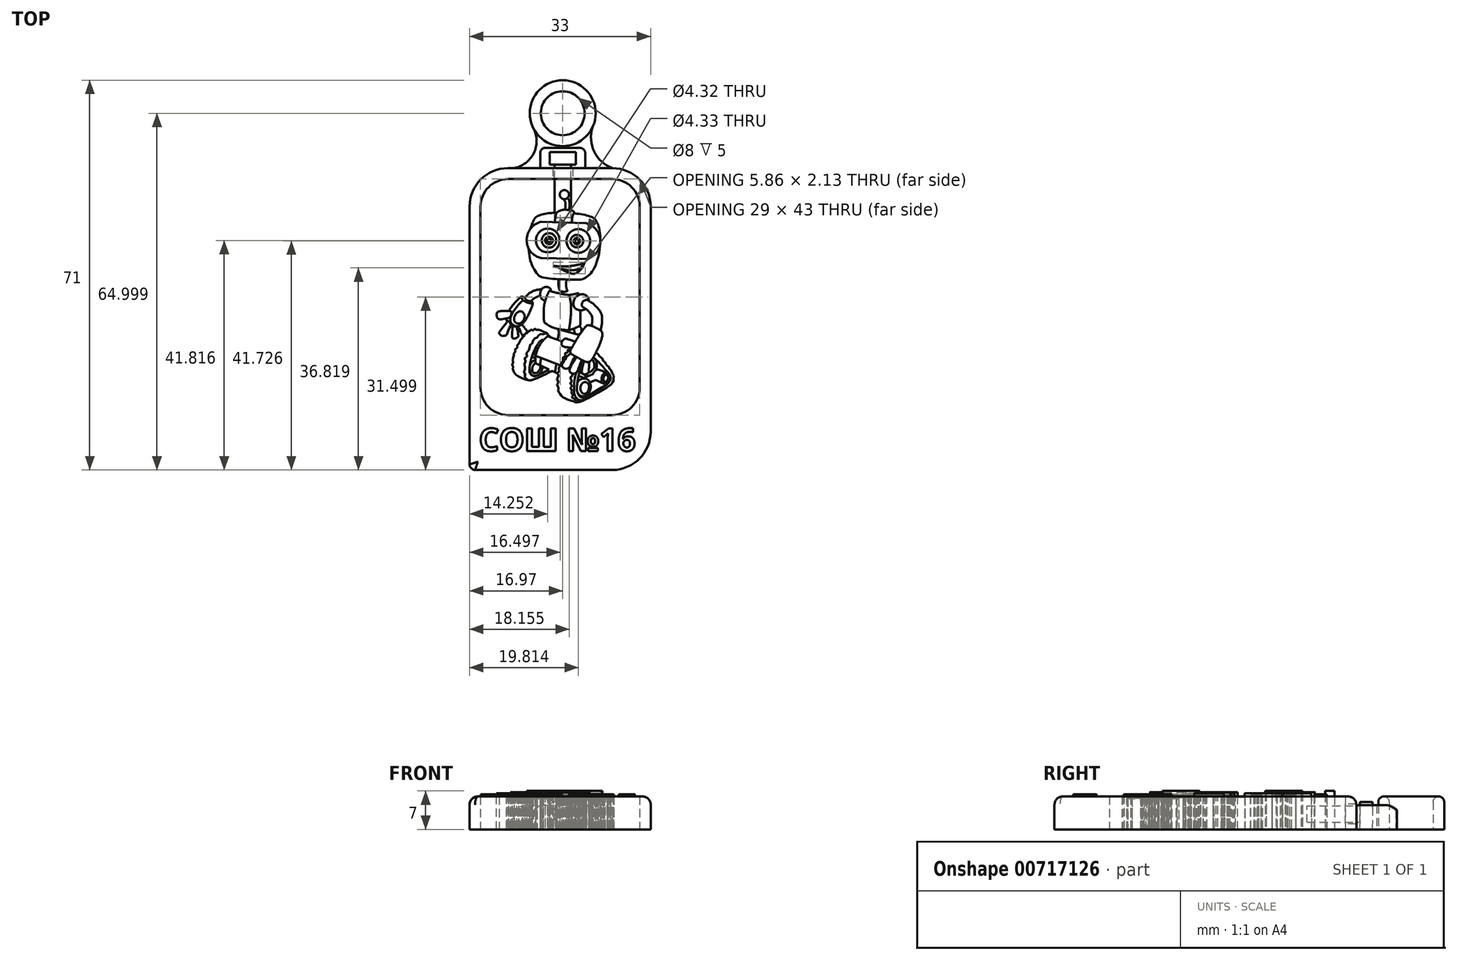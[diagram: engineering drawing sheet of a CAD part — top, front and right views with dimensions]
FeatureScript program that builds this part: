
annotation { "Feature Type Name" : "Feature", "Feature Type Description" : "" }
export const myFeature = defineFeature(function(context is Context, id is Id, definition is map)
    precondition{}
    {
        {
            var Q0;
            Q0=qCreatedBy(makeId("Top.planeOp"),FACE);
            var sketch = newSketch(context, id + "F0", { "sketchPlane" : qUnion([Q0])});
            skCircle(sketch, "E0", {"center": v(0.3, 18.7) * mm, "radius": 0.83 * mm});
            skFitSpline(sketch, "E1", {"points": [v(0.12, 17.9) * mm, v(0.47, 17.38) * mm, v(0.44, 15.96) * mm], "startDerivative": vector(0.9, -1.14) * mm, "endDerivative": vector(-0.07, -2.7) * mm});
            skFitSpline(sketch, "E2", {"points": [v(0.91, 18.15) * mm, v(1.19, 17.54) * mm, v(1.2, 15.9) * mm], "startDerivative": vector(0.78, -1.27) * mm, "endDerivative": vector(-0.02, -2.88) * mm});
            skCircle(sketch, "E3", {"center": v(-2.5, 10.36) * mm, "radius": 0.33 * mm});
            skCircle(sketch, "E4", {"center": v(-2.5, 10.36) * mm, "radius": 0.69 * mm});
            skCircle(sketch, "E5", {"center": v(-2.5, 10.36) * mm, "radius": 1.31 * mm});
            skCircle(sketch, "E6", {"center": v(2.58, 10.23) * mm, "radius": 0.33 * mm});
            skCircle(sketch, "E7", {"center": v(2.58, 10.23) * mm, "radius": 0.59 * mm});
            skCircle(sketch, "E8", {"center": v(2.58, 10.23) * mm, "radius": 1.15 * mm});
            skCircle(sketch, "E9", {"center": v(2.84, 10.27) * mm, "radius": 2.16 * mm});
            skPoint(sketch, "E9.first.point", {"position": v(4.19, 8.57) * mm});
            skPoint(sketch, "E9.second.point", {"position": v(4.6, 11.53) * mm});
            skPoint(sketch, "E9.third.point", {"position": v(0.83, 11.06) * mm});
            skCircle(sketch, "E10", {"center": v(-2.72, 10.36) * mm, "radius": 2.16 * mm});
            skPoint(sketch, "E10.first.point", {"position": v(-4.8, 10.92) * mm});
            skPoint(sketch, "E10.second.point", {"position": v(-3.27, 8.27) * mm});
            skPoint(sketch, "E10.third.point", {"position": v(-0.74, 11.23) * mm});
            skArc(sketch, "E11", {"start": v(-3.9, 13.75) * mm, "mid": v(-6.58, 10.45) * mm, "end": v(-3.92, 7.14) * mm});
            skArc(sketch, "E12", {"start": v(4.26, 6.95) * mm, "mid": v(6.85, 10.2) * mm, "end": v(4.28, 13.48) * mm});
            skLineSegment(sketch, "E13", {"start": v(-3.9, 13.75) * mm, "end": v(4.28, 13.48) * mm});
            skLineSegment(sketch, "E14", {"start": v(4.26, 6.95) * mm, "end": v(-3.92, 7.14) * mm});
            skFitSpline(sketch, "E15", {"points": [v(-1.45, 13.67) * mm, v(-1.34, 14.52) * mm, v(-1.2, 15.22) * mm, v(-1.1, 15.44) * mm, v(-0.38, 15.83) * mm, v(0.25, 15.96) * mm, v(0.44, 15.96) * mm, v(1.6, 15.83) * mm, v(2.03, 15.62) * mm, v(2.14, 15.45) * mm, v(2.16, 15.35) * mm, v(2.13, 15.29) * mm, v(2.02, 15.27) * mm, v(1.88, 15.13) * mm, v(1.62, 13.57) * mm], "startDerivative": vector(0.63, 8.93) * mm, "endDerivative": vector(-1.73, -15.25) * mm});
            skFitSpline(sketch, "E16", {"points": [v(-5.9, 12.47) * mm, v(-5.25, 14.1) * mm, v(-4.61, 14.77) * mm, v(-2.92, 15.27) * mm, v(-1.14, 15.4) * mm], "startDerivative": vector(2.4, 6.84) * mm, "endDerivative": vector(6.47, 0.13) * mm});
            skFitSpline(sketch, "E17", {"points": [v(-6.22, 8.92) * mm, v(-5.75, 6.26) * mm, v(-4.69, 4.3) * mm, v(-4.2, 3.84) * mm, v(-2.5, 3.43) * mm, v(0.92, 3.23) * mm, v(3.35, 3.25) * mm, v(4.25, 3.62) * mm, v(5.1, 4.38) * mm, v(6.1, 6.12) * mm, v(6.84, 10.02) * mm, v(6.6, 12.73) * mm, v(6.13, 13.9) * mm, v(5.7, 14.4) * mm, v(5.07, 14.7) * mm, v(3.8, 15.05) * mm, v(2.13, 15.29) * mm], "startDerivative": vector(2.92, -34.4) * mm, "endDerivative": vector(-27.68, 3.02) * mm});
            skFitSpline(sketch, "E18", {"points": [v(-1.75, 5.73) * mm, v(0.46, 5.61) * mm, v(2.53, 5.87) * mm, v(3.44, 6.09) * mm, v(4.12, 6.42) * mm], "startDerivative": vector(6.97, -0.72) * mm, "endDerivative": vector(3.62, 2.06) * mm});
            skFitSpline(sketch, "E19", {"points": [v(-1.75, 5.73) * mm, v(-0.96, 5.5) * mm, v(-0.2, 5.08) * mm, v(0.9, 4.56) * mm, v(1.74, 4.3) * mm, v(2.27, 4.34) * mm, v(3.1, 4.89) * mm, v(3.8, 5.89) * mm, v(3.9, 6.18) * mm, v(4.12, 6.42) * mm], "startDerivative": vector(7, -1.48) * mm, "endDerivative": vector(3.55, 3.32) * mm});
            skFitSpline(sketch, "E20", {"points": [v(-0.14, 5.6) * mm, v(-0.03, 5.1) * mm], "startDerivative": vector(0.1, -0.52) * mm, "endDerivative": vector(0.1, -0.52) * mm});
            skFitSpline(sketch, "E21", {"points": [v(-0.03, 5.1) * mm, v(0.8, 4.95) * mm, v(1.93, 4.94) * mm, v(2.96, 5.2) * mm, v(3.46, 5.49) * mm], "startDerivative": vector(3.26, -0.68) * mm, "endDerivative": vector(2.23, 1.53) * mm});
            skFitSpline(sketch, "E22", {"points": [v(3.46, 5.49) * mm, v(3.57, 6.14) * mm], "startDerivative": vector(0.1, 0.65) * mm, "endDerivative": vector(0.1, 0.65) * mm});
            skFitSpline(sketch, "E23", {"points": [v(-0.7, 1.73) * mm, v(-1, 1.68) * mm, v(-1.52, 1.57) * mm, v(-2.17, 1.34) * mm, v(-2.34, 1.21) * mm, v(-1.9, 1.02) * mm, v(-0.46, 0.67) * mm, v(0.7, 0.47) * mm, v(1.12, 0.44) * mm, v(1.38, 0.45) * mm, v(1.8, 0.52) * mm, v(2.6, 0.69) * mm, v(2.77, 0.77) * mm, v(2.73, 0.86) * mm, v(2.54, 1.01) * mm, v(1.61, 1.37) * mm, v(0.7, 1.58) * mm], "startDerivative": vector(-6.76, -0.7) * mm, "endDerivative": vector(-10.1, 1.55) * mm});
            skFitSpline(sketch, "E24", {"points": [v(-0.76, 3.3) * mm, v(-0.8, 2.67) * mm, v(-0.75, 1.97) * mm, v(-0.57, 1.3) * mm, v(-0.45, 1.13) * mm], "startDerivative": vector(-0.24, -2.28) * mm, "endDerivative": vector(0.93, -0.81) * mm});
            skFitSpline(sketch, "E25", {"points": [v(0.74, 3.24) * mm, v(0.64, 2.9) * mm, v(0.6, 2.27) * mm, v(0.66, 1.73) * mm, v(0.81, 1.31) * mm, v(0.85, 1.18) * mm], "startDerivative": vector(-0.63, -1.61) * mm, "endDerivative": vector(-0.1, -1.03) * mm});
            skFitSpline(sketch, "E26", {"points": [v(-0.45, 1.13) * mm, v(-0.22, 1.06) * mm, v(0.33, 1.01) * mm, v(0.7, 1.09) * mm, v(0.85, 1.18) * mm], "startDerivative": vector(0.96, -0.5) * mm, "endDerivative": vector(0.36, 0.85) * mm});
            skFitSpline(sketch, "E27", {"points": [v(1.12, 0.44) * mm, v(1.24, 0.2) * mm, v(1.38, -0.41) * mm, v(1.53, -1.74) * mm, v(1.38, -4.22) * mm, v(1.12, -5.92) * mm, v(1.04, -6) * mm, v(0.22, -5.93) * mm, v(-1.19, -5.72) * mm, v(-2.27, -5.29) * mm, v(-3.16, -4.72) * mm, v(-3.32, -4.57) * mm, v(-3.39, -4.44) * mm, v(-3.47, -3.34) * mm, v(-3.46, -2.3) * mm, v(-3.3, -1.07) * mm, v(-2.8, 0.44) * mm, v(-2.44, 1.14) * mm, v(-2.33, 1.25) * mm], "startDerivative": vector(7.24, -3.6) * mm, "endDerivative": vector(4.32, 3.3) * mm});
            skFitSpline(sketch, "E28", {"points": [v(1.04, -6) * mm, v(1.39, -5.9) * mm, v(2.36, -5.56) * mm, v(2.9, -5.32) * mm, v(3.1, -5.2) * mm, v(3.18, -5) * mm, v(3.21, -4.58) * mm, v(3.19, -2.37) * mm], "startDerivative": vector(2.66, 0.6) * mm, "endDerivative": vector(-0.15, 9.68) * mm});
            skFitSpline(sketch, "E29", {"points": [v(2.77, 0.79) * mm, v(2.82, 0.7) * mm, v(2.87, 0.37) * mm], "startDerivative": vector(0.07, -0.11) * mm, "endDerivative": vector(0.06, -0.59) * mm});
            skFitSpline(sketch, "E30", {"points": [v(-3.17, -0.58) * mm, v(-3.39, -0.55) * mm, v(-3.82, -0.28) * mm, v(-4.1, 0.29) * mm, v(-4.04, 1.06) * mm, v(-3.73, 1.58) * mm, v(-3.27, 1.86) * mm, v(-2.76, 1.88) * mm, v(-2.36, 1.68) * mm, v(-2.22, 1.54) * mm, v(-2.11, 1.36) * mm], "startDerivative": vector(-2.86, 0.03) * mm, "endDerivative": vector(1.55, -2.75) * mm});
            skFitSpline(sketch, "E31", {"points": [v(4.2, -2.1) * mm, v(3.83, -2.28) * mm, v(3.38, -2.4) * mm, v(3.19, -2.37) * mm, v(2.56, -2.2) * mm, v(2.14, -1.83) * mm, v(1.93, -1.09) * mm, v(2.2, -0.2) * mm, v(2.56, 0.19) * mm, v(2.87, 0.37) * mm, v(3.37, 0.54) * mm, v(4, 0.47) * mm, v(4.49, 0.12) * mm, v(4.73, -0.35) * mm, v(4.76, -0.66) * mm], "startDerivative": vector(-4.5, -3.3) * mm, "endDerivative": vector(0.01, -5.32) * mm});
            skFitSpline(sketch, "E32", {"points": [v(-3.48, -3.22) * mm, v(-1.78, -4.06) * mm, v(1.36, -4.43) * mm, v(3.2, -3.79) * mm], "startDerivative": vector(4.9, -3.02) * mm, "endDerivative": vector(5.37, 2.7) * mm});
            skFitSpline(sketch, "E33", {"points": [v(-3.84, 1.46) * mm, v(-4.94, 1.3) * mm, v(-6.15, 0.68) * mm, v(-6.87, -0.09) * mm], "startDerivative": vector(-3.3, -0.27) * mm, "endDerivative": vector(-2.02, -2.53) * mm});
            skFitSpline(sketch, "E34", {"points": [v(-4.08, 0.2) * mm, v(-4.4, 0.17) * mm, v(-5.23, -0.2) * mm, v(-5.69, -0.66) * mm], "startDerivative": vector(-1.12, 0.03) * mm, "endDerivative": vector(-1.09, -1.4) * mm});
            skFitSpline(sketch, "E35", {"points": [v(-6.87, -0.09) * mm, v(-6.78, -0.35) * mm, v(-6.22, -0.66) * mm, v(-5.8, -0.72) * mm, v(-5.69, -0.66) * mm], "startDerivative": vector(0.17, -1.2) * mm, "endDerivative": vector(0.62, 0.48) * mm});
            skFitSpline(sketch, "E36", {"points": [v(-5.65, -0.61) * mm, v(-5.52, -0.96) * mm, v(-5.55, -1.08) * mm, v(-5.79, -1.1) * mm, v(-6.43, -0.95) * mm, v(-7.26, -0.55) * mm, v(-7.32, -0.47) * mm, v(-7.53, 0.04) * mm, v(-7.46, 0.1) * mm, v(-6.84, -0.04) * mm], "startDerivative": vector(1.46, -3.36) * mm, "endDerivative": vector(5.12, -1.6) * mm});
            skFitSpline(sketch, "E37", {"points": [v(-7.4, 0.1) * mm, v(-7.53, 0.13) * mm, v(-7.7, 0.04) * mm, v(-8.25, -0.5) * mm, v(-9.37, -1.76) * mm, v(-9.7, -2.26) * mm, v(-9.85, -2.52) * mm], "startDerivative": vector(-1.54, 0.55) * mm, "endDerivative": vector(-1.06, -1.93) * mm});
            skFitSpline(sketch, "E38", {"points": [v(-5.54, -0.9) * mm, v(-5.48, -1.03) * mm, v(-5.48, -1.23) * mm, v(-6.29, -3.27) * mm, v(-6.98, -4.42) * mm, v(-7.46, -4.94) * mm, v(-8, -5.24) * mm, v(-8.74, -5.2) * mm, v(-9.4, -4.73) * mm, v(-9.52, -3.77) * mm, v(-9.1, -2.76) * mm, v(-8.38, -1.75) * mm, v(-7.3, -0.5) * mm], "startDerivative": vector(2.07, -4.05) * mm, "endDerivative": vector(10.06, 11.15) * mm});
            skEllipse(sketch, "E39", {"center": v(-7.91, -3.7) * mm, "majorRadius": 1.17 * mm, "minorRadius": 0.9 * mm, "majorAxis": v(0.45, 0.9)});
            skFitSpline(sketch, "E40", {"points": [v(-9.85, -3.75) * mm, v(-11.14, -4) * mm, v(-11.6, -4) * mm, v(-11.94, -3.67) * mm, v(-12.06, -3) * mm, v(-11.93, -2.73) * mm, v(-11.68, -2.58) * mm, v(-11.07, -2.52) * mm, v(-9.85, -2.52) * mm], "startDerivative": vector(-8, -1.73) * mm, "endDerivative": vector(7.43, -0.04) * mm});
            skFitSpline(sketch, "E41", {"points": [v(-9.85, -3.75) * mm, v(-9.6, -3.57) * mm, v(-9.39, -3.2) * mm, v(-9.34, -2.7) * mm, v(-9.52, -2.52) * mm, v(-9.85, -2.52) * mm], "startDerivative": vector(1.43, 0.8) * mm, "endDerivative": vector(-1.85, -0.22) * mm});
            skFitSpline(sketch, "E42", {"points": [v(4.38, -0.46) * mm, v(4.76, -0.66) * mm, v(5.4, -1.08) * mm, v(6.04, -1.64) * mm, v(6.54, -2.18) * mm, v(7.06, -3.11) * mm, v(7.16, -4.62) * mm, v(6.9, -6.06) * mm], "startDerivative": vector(3.69, -1.9) * mm, "endDerivative": vector(-2.34, -7.83) * mm});
            skFitSpline(sketch, "E43", {"points": [v(3.66, -1.78) * mm, v(4.2, -2.1) * mm, v(4.87, -2.73) * mm, v(5.32, -3.49) * mm, v(5.34, -4.62) * mm, v(5.24, -5.2) * mm], "startDerivative": vector(2.71, -1.62) * mm, "endDerivative": vector(-1.18, -2.93) * mm});
            skFitSpline(sketch, "E44", {"points": [v(6.9, -6.06) * mm, v(7.16, -6.34) * mm, v(7.23, -6.83) * mm, v(6.74, -8.54) * mm, v(5.58, -10.93) * mm, v(5.1, -11.56) * mm, v(4.63, -11.8) * mm, v(3.71, -11.54) * mm, v(1.8, -10.47) * mm, v(1.45, -10.2) * mm, v(1.37, -9.71) * mm, v(1.59, -9.3) * mm, v(2.54, -7.66) * mm, v(3.61, -6.06) * mm, v(4.2, -5.3) * mm, v(4.43, -5.1) * mm, v(5.24, -5.2) * mm, v(6.9, -6.06) * mm]});
            skFitSpline(sketch, "E45", {"points": [v(2.3, -8.07) * mm, v(0.6, -7.54) * mm, v(0.42, -7.54) * mm, v(0, -7.87) * mm, v(-0.23, -8.54) * mm, v(-0.05, -8.88) * mm, v(0.5, -9.08) * mm, v(1.68, -9.17) * mm], "startDerivative": vector(-9.45, 3.1) * mm, "endDerivative": vector(6.78, -0.26) * mm});
            skFitSpline(sketch, "E46", {"points": [v(3.87, -11.61) * mm, v(3.62, -12.64) * mm, v(3.48, -13.45) * mm, v(3.59, -13.84) * mm, v(3.9, -14.03) * mm, v(4.39, -13.95) * mm, v(4.76, -13.6) * mm, v(4.76, -13.41) * mm, v(4.85, -11.74) * mm], "startDerivative": vector(-1.62, -6.5) * mm, "endDerivative": vector(0.7, 10.55) * mm});
            skFitSpline(sketch, "E47", {"points": [v(3.5, -11.43) * mm, v(2.64, -13.52) * mm, v(2.48, -13.76) * mm, v(1.9, -13.9) * mm, v(1.36, -13.66) * mm, v(1.26, -13.3) * mm, v(1.44, -12.67) * mm, v(2.53, -10.9) * mm], "startDerivative": vector(-4.72, -11.44) * mm, "endDerivative": vector(5.93, 9.05) * mm});
            skFitSpline(sketch, "E48", {"points": [v(2.27, -10.74) * mm, v(1.68, -11.81) * mm, v(1.26, -12.74) * mm, v(0.92, -12.97) * mm, v(0.34, -12.97) * mm, v(-0.14, -12.43) * mm, v(0.2, -11.65) * mm, v(0.86, -10.73) * mm, v(1.45, -10.2) * mm], "startDerivative": vector(-3.77, -6.76) * mm, "endDerivative": vector(4.2, 4.03) * mm});
            skFitSpline(sketch, "E49", {"points": [v(3.66, -1.78) * mm, v(3.48, -1.45) * mm, v(3.71, -0.73) * mm, v(4.38, -0.46) * mm], "startDerivative": vector(-0.94, 1.03) * mm, "endDerivative": vector(1.87, 0.43) * mm});
            skFitSpline(sketch, "E50", {"points": [v(1.6, -9.27) * mm, v(1.43, -9.26) * mm, v(1.38, -9.44) * mm, v(0.97, -9.54) * mm, v(0.86, -10.03) * mm, v(0.46, -10.2) * mm, v(0.48, -10.7) * mm, v(0.05, -10.97) * mm, v(0.07, -11.56) * mm, v(-0.23, -11.9) * mm, v(-0.38, -12.43) * mm, v(-0.7, -12.82) * mm, v(-0.7, -13.5) * mm, v(-0.98, -13.83) * mm, v(-0.79, -14.3) * mm, v(-1.05, -14.84) * mm, v(-0.8, -15.5) * mm, v(-1.05, -15.84) * mm, v(-0.76, -16.5) * mm, v(-0.84, -16.9) * mm, v(-0.46, -17.65) * mm, v(0.2, -18.28) * mm, v(2.04, -19.01) * mm, v(3.13, -19.05) * mm, v(8.56, -16.08) * mm, v(9.01, -15.65) * mm, v(9.15, -15.34) * mm, v(9.27, -15.14) * mm, v(9.21, -14.97) * mm, v(9.34, -14.75) * mm, v(9.22, -14.49) * mm, v(9.3, -14.28) * mm, v(9.09, -13.91) * mm, v(9.1, -13.77) * mm, v(8.78, -13.4) * mm, v(8.8, -13.21) * mm, v(8.42, -12.89) * mm, v(8.5, -12.75) * mm, v(8.04, -12.43) * mm, v(8.07, -12.32) * mm, v(7.7, -11.97) * mm, v(7.73, -11.8) * mm, v(7.36, -11.56) * mm, v(7.37, -11.31) * mm, v(7, -11.1) * mm, v(7.02, -10.98) * mm, v(6.72, -10.73) * mm, v(6.7, -10.61) * mm, v(6.38, -10.44) * mm, v(6.38, -10.26) * mm, v(6.04, -10.08) * mm], "startDerivative": vector(-15.2, 2.24) * mm, "endDerivative": vector(-28.52, 9.44) * mm});
            skFitSpline(sketch, "E51", {"points": [v(1.67, -13.87) * mm, v(1.76, -14.28) * mm, v(1.38, -14.65) * mm, v(1.68, -15.3) * mm, v(1.38, -15.62) * mm, v(1.68, -16.15) * mm, v(1.38, -16.5) * mm, v(1.68, -16.92) * mm, v(1.59, -17.5) * mm, v(1.87, -17.85) * mm, v(1.68, -18.2) * mm, v(2.3, -18.66) * mm, v(2.48, -18.94) * mm, v(3.13, -19.05) * mm], "startDerivative": vector(3.43, -6.3) * mm, "endDerivative": vector(10.14, -0.04) * mm});
            skFitSpline(sketch, "E52", {"points": [v(2.48, -13.76) * mm, v(2.24, -14.48) * mm, v(2.06, -16.55) * mm, v(2.2, -17.86) * mm, v(2.9, -18.7) * mm, v(3.92, -18.64) * mm, v(4.67, -18.36) * mm], "startDerivative": vector(-1.23, -4.5) * mm, "endDerivative": vector(4.87, 2.34) * mm});
            skFitSpline(sketch, "E53", {"points": [v(3.71, -11.54) * mm, v(3.17, -13.15) * mm, v(2.74, -15.07) * mm, v(2.68, -17.36) * mm, v(3.27, -18.17) * mm, v(4.2, -18.1) * mm, v(7.11, -16.42) * mm, v(8.4, -15.53) * mm, v(8.72, -14.56) * mm, v(8.07, -13.52) * mm, v(6.64, -11.91) * mm, v(5.58, -10.93) * mm], "startDerivative": vector(-6.92, -17.06) * mm, "endDerivative": vector(-12.58, 10.17) * mm});
            skFitSpline(sketch, "E54", {"points": [v(2.65, -15.66) * mm, v(3.13, -15.01) * mm, v(4.2, -14.82) * mm, v(4.87, -15.37) * mm, v(5.1, -16.33) * mm, v(4.73, -17.48) * mm, v(4.2, -17.94) * mm, v(3.71, -18.07) * mm, v(3.13, -17.92) * mm, v(2.68, -17.36) * mm], "startDerivative": vector(3.07, 6.78) * mm, "endDerivative": vector(-2.95, 6.13) * mm});
            skLineSegment(sketch, "E55", {"start": v(4.2, -14.82) * mm, "end": v(2.88, -14.32) * mm});
            skLineSegment(sketch, "E56", {"start": v(4.95, -15.52) * mm, "end": v(5.98, -15.08) * mm});
            skLineSegment(sketch, "E57", {"start": v(5.98, -15.08) * mm, "end": v(7.58, -15.75) * mm});
            skEllipse(sketch, "E58", {"center": v(4.01, -16.5) * mm, "majorRadius": 1.09 * mm, "minorRadius": 0.78 * mm, "majorAxis": v(0.16, 0.99)});
            skEllipse(sketch, "E59", {"center": v(7.83, -14.75) * mm, "majorRadius": 0.63 * mm, "minorRadius": 0.45 * mm, "majorAxis": v(0.27, 0.96)});
            skEllipse(sketch, "E60", {"center": v(7.83, -14.75) * mm, "majorRadius": 1.03 * mm, "minorRadius": 0.75 * mm, "majorAxis": v(-0.24, -0.97)});
            skFitSpline(sketch, "E61", {"points": [v(5.98, -15.08) * mm, v(5.62, -14.73) * mm, v(5.5, -14.2) * mm, v(5.65, -13.69) * mm, v(5.98, -13.32) * mm, v(6.33, -13.16) * mm, v(6.48, -13.17) * mm], "startDerivative": vector(-2.22, 1.68) * mm, "endDerivative": vector(1.4, -0.29) * mm});
            skLineSegment(sketch, "E62", {"start": v(6.48, -13.17) * mm, "end": v(8.14, -13.77) * mm});
            skLineSegment(sketch, "E63", {"start": v(3.79, -14.66) * mm, "end": v(5.52, -14) * mm});
            skFitSpline(sketch, "E64", {"points": [v(3.04, -13.64) * mm, v(4.2, -14.23) * mm, v(4.52, -14.3) * mm, v(4.9, -14.24) * mm], "startDerivative": vector(2.74, -1.49) * mm, "endDerivative": vector(1.52, 0.33) * mm});
            skFitSpline(sketch, "E65", {"points": [v(5.8, -11.1) * mm, v(6.2, -11.92) * mm, v(6.11, -13.04) * mm, v(5.98, -13.32) * mm], "startDerivative": vector(1.4, -1.95) * mm, "endDerivative": vector(-0.64, -1) * mm});
            skFitSpline(sketch, "E66", {"points": [v(3.43, -12.3) * mm, v(3.4, -12.94) * mm, v(3.48, -13.45) * mm], "startDerivative": vector(-0.12, -1.25) * mm, "endDerivative": vector(0.22, -1.05) * mm});
            skFitSpline(sketch, "E67", {"points": [v(5.26, -11.4) * mm, v(5.57, -11.6) * mm, v(5.77, -12.6) * mm, v(5.38, -13.32) * mm, v(4.94, -13.63) * mm, v(4.73, -13.65) * mm], "startDerivative": vector(1.96, -0.71) * mm, "endDerivative": vector(-1.59, 0.06) * mm});
            skLineSegment(sketch, "E68", {"start": v(-2.77, -7.1) * mm, "end": v(-0.11, -8.05) * mm});
            skFitSpline(sketch, "E69", {"points": [v(-2.77, -7.1) * mm, v(-3.76, -8.1) * mm, v(-4.58, -9.48) * mm, v(-4.98, -11) * mm, v(-4.98, -12.02) * mm], "startDerivative": vector(-4.13, -3.72) * mm, "endDerivative": vector(0.28, -4.5) * mm});
            skLineSegment(sketch, "E70", {"start": v(-4.98, -12.02) * mm, "end": v(-0.98, -13.83) * mm});
            skLineSegment(sketch, "E71", {"start": v(-4.94, -10.69) * mm, "end": v(-0.38, -12.43) * mm});
            skFitSpline(sketch, "E72", {"points": [v(-3.9, -11.08) * mm, v(-4.04, -11.64) * mm, v(-4.07, -12.43) * mm], "startDerivative": vector(-0.58, -1.59) * mm, "endDerivative": vector(0.13, -1.26) * mm});
            skFitSpline(sketch, "E73", {"points": [v(-1.11, -12.15) * mm, v(-1.3, -12.88) * mm, v(-1.33, -13.68) * mm], "startDerivative": vector(-0.59, -1.61) * mm, "endDerivative": vector(0.18, -1.44) * mm});
            skFitSpline(sketch, "E74", {"points": [v(-10.25, -3.83) * mm, v(-10.23, -4.14) * mm, v(-10.1, -4.43) * mm], "startDerivative": vector(0, -0.64) * mm, "endDerivative": vector(0.32, -0.56) * mm});
            skFitSpline(sketch, "E75", {"points": [v(-10.1, -4.43) * mm, v(-11.55, -6.34) * mm, v(-11.6, -6.47) * mm, v(-11.5, -6.69) * mm, v(-11.18, -6.98) * mm, v(-10.8, -7.04) * mm, v(-10.32, -6.92) * mm, v(-10.21, -6.75) * mm, v(-9.48, -5.02) * mm, v(-9.5, -4.87) * mm, v(-9.71, -4.49) * mm, v(-9.84, -4.37) * mm, v(-10.04, -4.37) * mm, v(-10.1, -4.43) * mm]});
            skFitSpline(sketch, "E76", {"points": [v(-9.48, -5.02) * mm, v(-9, -5.24) * mm, v(-8.42, -5.34) * mm, v(-8, -5.24) * mm], "startDerivative": vector(1.34, -0.74) * mm, "endDerivative": vector(1.3, 0.44) * mm});
            skFitSpline(sketch, "E77", {"points": [v(-9.15, -5.18) * mm, v(-9.24, -7.14) * mm, v(-9.2, -7.4) * mm, v(-8.88, -7.52) * mm, v(-8.59, -7.46) * mm, v(-8.19, -7.2) * mm, v(-8.09, -6.96) * mm, v(-8.42, -5.34) * mm], "startDerivative": vector(-0.42, -9.45) * mm, "endDerivative": vector(-2.16, 8.56) * mm});
            skFitSpline(sketch, "E78", {"points": [v(-2.33, -7.25) * mm, v(-2.32, -7.1) * mm, v(-2.67, -6.94) * mm, v(-2.67, -6.77) * mm, v(-4.55, -5.92) * mm, v(-4.84, -5.92) * mm, v(-5.1, -5.76) * mm, v(-5.47, -6.03) * mm, v(-5.8, -5.9) * mm, v(-6.01, -6.18) * mm, v(-6.3, -6.17) * mm, v(-6.48, -6.55) * mm, v(-6.88, -6.62) * mm, v(-7, -7.05) * mm, v(-7.35, -7.14) * mm, v(-7.42, -7.6) * mm, v(-7.8, -7.83) * mm, v(-7.86, -8.37) * mm, v(-8.27, -8.66) * mm, v(-8.27, -9.1) * mm, v(-8.65, -9.47) * mm, v(-8.68, -10.02) * mm, v(-8.97, -10.35) * mm, v(-8.87, -10.76) * mm, v(-9.15, -11.23) * mm, v(-9, -11.77) * mm, v(-9.21, -12.18) * mm, v(-9.02, -12.66) * mm, v(-9.1, -13.05) * mm, v(-8.66, -14) * mm, v(-8.24, -14.36) * mm, v(-6.87, -14.98) * mm, v(-5.82, -15.11) * mm, v(-1.92, -13.4) * mm], "startDerivative": vector(4.57, 10.26) * mm, "endDerivative": vector(54.83, 27.76) * mm});
            skFitSpline(sketch, "E79", {"points": [v(-8.12, -5.28) * mm, v(-7.37, -6.88) * mm, v(-7.23, -6.96) * mm, v(-6.96, -6.94) * mm], "startDerivative": vector(1.52, -3.53) * mm, "endDerivative": vector(1.33, 0.21) * mm});
            skFitSpline(sketch, "E80", {"points": [v(-7.46, -4.94) * mm, v(-7.05, -5.44) * mm, v(-6.6, -6.02) * mm, v(-6.53, -6.13) * mm, v(-6.52, -6.4) * mm, v(-6.6, -6.58) * mm], "startDerivative": vector(1.44, -1.7) * mm, "endDerivative": vector(-0.68, -1.04) * mm});
            skFitSpline(sketch, "E81", {"points": [v(-2.67, -6.77) * mm, v(-3.04, -6.63) * mm, v(-3.34, -6.55) * mm, v(-3.72, -6.77) * mm, v(-4, -6.66) * mm, v(-4.22, -6.96) * mm, v(-4.5, -6.96) * mm, v(-4.66, -7.33) * mm, v(-5.04, -7.4) * mm, v(-5.13, -7.8) * mm, v(-5.49, -7.92) * mm, v(-5.56, -8.4) * mm, v(-5.9, -8.54) * mm, v(-5.94, -9.12) * mm, v(-6.26, -9.37) * mm, v(-6.2, -9.85) * mm, v(-6.7, -10.26) * mm, v(-6.48, -10.86) * mm, v(-6.93, -11.14) * mm, v(-6.74, -11.68) * mm, v(-7.05, -12.02) * mm, v(-6.75, -12.47) * mm, v(-7.07, -12.82) * mm, v(-6.84, -13.2) * mm, v(-7.05, -13.67) * mm, v(-6.78, -14.01) * mm, v(-7.06, -14.29) * mm, v(-6.65, -14.67) * mm, v(-6.61, -14.96) * mm, v(-6.17, -15.15) * mm], "startDerivative": vector(-11.53, 3.84) * mm, "endDerivative": vector(16.6, -3.55) * mm});
            skFitSpline(sketch, "E82", {"points": [v(-2.48, -13.16) * mm, v(-4.42, -14.13) * mm, v(-5.25, -14.35) * mm, v(-5.96, -13.83) * mm, v(-5.98, -12.31) * mm, v(-5.38, -10.14) * mm, v(-4.22, -8.1) * mm, v(-3.76, -7.79) * mm, v(-3.5, -7.79) * mm], "startDerivative": vector(-12.89, -6.58) * mm, "endDerivative": vector(4.5, -0.52) * mm});
            skFitSpline(sketch, "E83", {"points": [v(-3.72, -12.6) * mm, v(-3.72, -12.97) * mm, v(-3.98, -13.62) * mm, v(-4.65, -14.24) * mm, v(-5.24, -14.3) * mm, v(-5.74, -14.02) * mm, v(-5.97, -13.44) * mm, v(-6.03, -12.64) * mm, v(-5.67, -11.88) * mm, v(-5.2, -11.5) * mm, v(-5, -11.43) * mm], "startDerivative": vector(0.38, -4.4) * mm, "endDerivative": vector(2.97, 0.62) * mm});
            skFitSpline(sketch, "E84", {"points": [v(-5.65, -10.9) * mm, v(-5.2, -11) * mm, v(-5, -11.19) * mm], "startDerivative": vector(0.57, -0.15) * mm, "endDerivative": vector(0.38, -0.44) * mm});
            skFitSpline(sketch, "E85", {"points": [v(-5.43, -10.26) * mm, v(-4.91, -10.55) * mm], "startDerivative": vector(0.52, -0.28) * mm, "endDerivative": vector(0.52, -0.28) * mm});
            skFitSpline(sketch, "E86", {"points": [v(-4.73, -8.82) * mm, v(-4.98, -9.84) * mm, v(-4.87, -10.35) * mm], "startDerivative": vector(-1.14, -2.41) * mm, "endDerivative": vector(0.44, -1.13) * mm});
            skFitSpline(sketch, "E87", {"points": [v(-0.82, -5.8) * mm, v(-0.85, -5.94) * mm, v(-0.7, -6.17) * mm, v(-0.77, -6.3) * mm, v(-0.68, -6.54) * mm, v(-0.77, -6.63) * mm, v(-0.67, -6.8) * mm, v(-0.8, -6.87) * mm, v(-0.7, -7.08) * mm, v(-0.84, -7.18) * mm, v(-0.81, -7.39) * mm, v(-0.97, -7.48) * mm, v(-1, -7.63) * mm, v(-1.2, -7.66) * mm], "startDerivative": vector(-1.06, -2.03) * mm, "endDerivative": vector(-3.33, 0.28) * mm});
            skFitSpline(sketch, "E88", {"points": [v(2.17, -5.64) * mm, v(2.1, -5.99) * mm, v(2.29, -6.55) * mm, v(2.76, -6.78) * mm, v(3.22, -6.6) * mm], "startDerivative": vector(-0.53, -1.47) * mm, "endDerivative": vector(1.55, 1.3) * mm});
            skFitSpline(sketch, "E89", {"points": [v(2.98, -5.29) * mm, v(3.3, -5.53) * mm, v(3.42, -5.95) * mm, v(3.3, -6.49) * mm], "startDerivative": vector(1.17, -0.65) * mm, "endDerivative": vector(-0.68, -1.55) * mm});
            skLineSegment(sketch, "E90", {"start": v(-0.82, -5.8) * mm, "end": v(2.58, -6.75) * mm});
            skFitSpline(sketch, "E91", {"points": [v(-4.99, -11.96) * mm, v(-5.32, -12.33) * mm, v(-5.56, -13.07) * mm, v(-5.48, -13.55) * mm, v(-5.21, -13.8) * mm, v(-4.76, -13.77) * mm, v(-4.3, -13.35) * mm, v(-4.1, -12.9) * mm, v(-4.1, -12.57) * mm, v(-4.12, -12.4) * mm], "startDerivative": vector(-3.02, -2.7) * mm, "endDerivative": vector(-0.42, 2.2) * mm});
            skSolve(sketch);
        }
        {
            var Q0;
            {var subQ1=sQuery(id+"F0.wireOp",EDGE,"E44");var subQ12=makeQuery(id+"F0.imprint","INTERSECT",VERTEX,{"derivedFrom":[sQuery(id+"F0.wireOp",EDGE,"E42"),subQ1]});Q0=makeQuery(id+"F0.imprint","IMPRINT",FACE,{"disambiguationData":[TD([[makeQuery(id+"F0.imprint","IMPRINT",EDGE,{"disambiguationData":[TD([[subQ12,-1.0]])],"derivedFrom":subQ1}),-1.0]])]});}
            var Q1;
            Q1=makeQuery(id+"F0.imprint","IMPRINT",FACE,{"disambiguationData":[TD([[makeQuery(id+"F0.imprint","IMPRINT",EDGE,{"derivedFrom":sQuery(id+"F0.wireOp",EDGE,"E9")}),-1.0]])]});
            var Q2;
            {var subQ0=sQuery(id+"F0.wireOp",EDGE,"E0");var subQ1=makeQuery(id+"F0.imprint","INTERSECT",VERTEX,{"derivedFrom":[subQ0,sQuery(id+"F0.wireOp",EDGE,"E1")]});Q2=makeQuery(id+"F0.imprint","IMPRINT",FACE,{"disambiguationData":[TD([[makeQuery(id+"F0.imprint","IMPRINT",EDGE,{"disambiguationData":[TD([[subQ1,-1.0]])],"derivedFrom":subQ0}),1.0]])]});}
            extrude(context, id + "F1", {"entities" : qUnion([Q0, Q1, Q2]), "depth" : 7 * mm, "offsetDistance" : 25 * mm});
        }
        {
            var Q0;
            {var subQ0=sQuery(id+"F0.wireOp",EDGE,"E45");var subQ1=sQuery(id+"F0.wireOp",EDGE,"E44");var subQ2=makeQuery(id+"F0.imprint","INTERSECT",VERTEX,{"disambiguationData":[OD(0.0)],"derivedFrom":[subQ1,subQ0]});Q0=makeQuery(id+"F0.imprint","IMPRINT",FACE,{"disambiguationData":[TD([[makeQuery(id+"F0.imprint","IMPRINT",EDGE,{"disambiguationData":[TD([[subQ2,1.0]])],"derivedFrom":subQ1}),1.0]])]});}
            var Q1;
            {var subQ0=sQuery(id+"F0.wireOp",EDGE,"E48");Q1=makeQuery(id+"F0.imprint","IMPRINT",FACE,{"disambiguationData":[TD([[makeQuery(id+"F0.imprint","IMPRINT",EDGE,{"derivedFrom":subQ0}),-1.0]])]});}
            var Q2;
            {var subQ0=sQuery(id+"F0.wireOp",EDGE,"E47");var subQ1=sQuery(id+"F0.wireOp",EDGE,"E44");var subQ2=makeQuery(id+"F0.imprint","INTERSECT",VERTEX,{"disambiguationData":[OD(0.0)],"derivedFrom":[subQ1,subQ0]});Q2=makeQuery(id+"F0.imprint","IMPRINT",FACE,{"disambiguationData":[TD([[makeQuery(id+"F0.imprint","IMPRINT",EDGE,{"disambiguationData":[TD([[subQ2,-1.0]])],"derivedFrom":subQ1}),1.0]])]});}
            var Q3;
            {var subQ0=sQuery(id+"F0.wireOp",EDGE,"E46");var subQ1=sQuery(id+"F0.wireOp",EDGE,"E44");var subQ2=makeQuery(id+"F0.imprint","INTERSECT",VERTEX,{"disambiguationData":[OD(0.0)],"derivedFrom":[subQ1,subQ0]});Q3=makeQuery(id+"F0.imprint","IMPRINT",FACE,{"disambiguationData":[TD([[makeQuery(id+"F0.imprint","IMPRINT",EDGE,{"disambiguationData":[TD([[subQ2,1.0]])],"derivedFrom":subQ1}),1.0]])]});}
            var Q4;
            {var subQ3=sQuery(id+"F0.wireOp",EDGE,"E49");Q4=makeQuery(id+"F0.imprint","IMPRINT",FACE,{"disambiguationData":[TD([[makeQuery(id+"F0.imprint","IMPRINT",EDGE,{"derivedFrom":subQ3}),1.0]])]});}
            var Q5;
            {var subQ3=sQuery(id+"F0.wireOp",EDGE,"E27");var subQ5=sQuery(id+"F0.wireOp",EDGE,"E23");var subQ6=makeQuery(id+"F0.imprint","INTERSECT",VERTEX,{"disambiguationData":[OD(1.0)],"derivedFrom":[subQ5,subQ3]});Q5=makeQuery(id+"F0.imprint","IMPRINT",FACE,{"disambiguationData":[TD([[makeQuery(id+"F0.imprint","IMPRINT",EDGE,{"disambiguationData":[TD([[subQ6,1.0]])],"derivedFrom":subQ5}),-1.0]])]});}
            var Q6;
            Q6=makeQuery(id+"F0.imprint","IMPRINT",FACE,{"disambiguationData":[TD([[makeQuery(id+"F0.imprint","IMPRINT",EDGE,{"derivedFrom":sQuery(id+"F0.wireOp",EDGE,"E39")}),-1.0]])]});
            var Q7;
            Q7=makeQuery(id+"F0.imprint","IMPRINT",FACE,{"disambiguationData":[TD([[makeQuery(id+"F0.imprint","IMPRINT",EDGE,{"derivedFrom":sQuery(id+"F0.wireOp",EDGE,"E3")}),1.0]])]});
            var Q8;
            Q8=makeQuery(id+"F0.imprint","IMPRINT",FACE,{"disambiguationData":[TD([[makeQuery(id+"F0.imprint","IMPRINT",EDGE,{"derivedFrom":sQuery(id+"F0.wireOp",EDGE,"E6")}),1.0]])]});
            var Q9;
            {var subQ0=sQuery(id+"F0.wireOp",EDGE,"E15");var subQ3=sQuery(id+"F0.wireOp",EDGE,"E13");var subQ4=makeQuery(id+"F0.imprint","INTERSECT",VERTEX,{"disambiguationData":[OD(0.0)],"derivedFrom":[subQ3,subQ0]});Q9=makeQuery(id+"F0.imprint","IMPRINT",FACE,{"disambiguationData":[TD([[makeQuery(id+"F0.imprint","IMPRINT",EDGE,{"disambiguationData":[TD([[subQ4,-1.0]])],"derivedFrom":subQ3}),1.0]])]});}
            extrude(context, id + "F2", {"entities" : qUnion([Q0, Q1, Q2, Q3, Q4, Q5, Q6, Q7, Q8, Q9]), "depth" : 6.8 * mm, "offsetDistance" : 25 * mm});
        }
        {
            var Q0;
            {var subQ4=sQuery(id+"F0.wireOp",EDGE,"E14");Q0=makeQuery(id+"F0.imprint","IMPRINT",FACE,{"disambiguationData":[TD([[makeQuery(id+"F0.imprint","IMPRINT",EDGE,{"derivedFrom":subQ4}),1.0]])]});}
            var Q1;
            {var subQ3=sQuery(id+"F0.wireOp",EDGE,"E16");Q1=makeQuery(id+"F0.imprint","IMPRINT",FACE,{"disambiguationData":[TD([[makeQuery(id+"F0.imprint","IMPRINT",EDGE,{"derivedFrom":subQ3}),-1.0]])]});}
            var Q2;
            {var subQ0=sQuery(id+"F0.wireOp",EDGE,"E13");var subQ1=sQuery(id+"F0.wireOp",EDGE,"E12");var subQ2=makeQuery(id+"F0.imprint","INTERSECT",VERTEX,{"derivedFrom":[subQ1,subQ0]});Q2=makeQuery(id+"F0.imprint","IMPRINT",FACE,{"disambiguationData":[TD([[makeQuery(id+"F0.imprint","IMPRINT",EDGE,{"disambiguationData":[TD([[subQ2,1.0]])],"derivedFrom":subQ1}),-1.0]])]});}
            var Q3;
            {var subQ5=sQuery(id+"F0.wireOp",EDGE,"E49");Q3=makeQuery(id+"F0.imprint","IMPRINT",FACE,{"disambiguationData":[TD([[makeQuery(id+"F0.imprint","IMPRINT",EDGE,{"derivedFrom":subQ5}),-1.0]])]});}
            var Q4;
            {var subQ5=sQuery(id+"F0.wireOp",EDGE,"E35");Q4=makeQuery(id+"F0.imprint","IMPRINT",FACE,{"disambiguationData":[TD([[makeQuery(id+"F0.imprint","IMPRINT",EDGE,{"derivedFrom":subQ5}),1.0]])]});}
            var Q5;
            Q5=makeQuery(id+"F0.imprint","IMPRINT",FACE,{"disambiguationData":[TD([[makeQuery(id+"F0.imprint","IMPRINT",EDGE,{"derivedFrom":sQuery(id+"F0.wireOp",EDGE,"E39")}),1.0]])]});
            var Q6;
            {var subQ0=sQuery(id+"F0.wireOp",EDGE,"E79");Q6=makeQuery(id+"F0.imprint","IMPRINT",FACE,{"disambiguationData":[TD([[makeQuery(id+"F0.imprint","IMPRINT",EDGE,{"derivedFrom":subQ0}),1.0]])]});}
            var Q7;
            {var subQ0=sQuery(id+"F0.wireOp",EDGE,"E77");Q7=makeQuery(id+"F0.imprint","IMPRINT",FACE,{"disambiguationData":[TD([[makeQuery(id+"F0.imprint","IMPRINT",EDGE,{"derivedFrom":subQ0}),1.0]])]});}
            var Q8;
            {var subQ0=sQuery(id+"F0.wireOp",EDGE,"E75");var subQ1=makeQuery(id+"F0.imprint","INTERSECT",VERTEX,{"derivedFrom":[sQuery(id+"F0.wireOp",EDGE,"E74"),subQ0]});Q8=makeQuery(id+"F0.imprint","IMPRINT",FACE,{"disambiguationData":[TD([[makeQuery(id+"F0.imprint","IMPRINT",EDGE,{"disambiguationData":[TD([[subQ1,-1.0]])],"derivedFrom":subQ0}),1.0]])]});}
            var Q9;
            {var subQ0=sQuery(id+"F0.wireOp",EDGE,"E41");Q9=makeQuery(id+"F0.imprint","IMPRINT",FACE,{"disambiguationData":[TD([[makeQuery(id+"F0.imprint","IMPRINT",EDGE,{"derivedFrom":subQ0}),1.0]])]});}
            var Q10;
            {var subQ1=sQuery(id+"F0.wireOp",EDGE,"E27");var subQ4=sQuery(id+"F0.wireOp",EDGE,"E28");var subQ6=makeQuery(id+"F0.imprint","INTERSECT",VERTEX,{"disambiguationData":[OD(1.0)],"derivedFrom":[subQ1,subQ4]});Q10=makeQuery(id+"F0.imprint","IMPRINT",FACE,{"disambiguationData":[TD([[makeQuery(id+"F0.imprint","IMPRINT",EDGE,{"disambiguationData":[TD([[subQ6,1.0]])],"derivedFrom":subQ1}),-1.0]])]});}
            var Q11;
            {var subQ0=sQuery(id+"F0.wireOp",EDGE,"E27");var subQ4=sQuery(id+"F0.wireOp",EDGE,"E23");var subQ6=makeQuery(id+"F0.imprint","INTERSECT",VERTEX,{"disambiguationData":[OD(0.0)],"derivedFrom":[subQ4,subQ0]});Q11=makeQuery(id+"F0.imprint","IMPRINT",FACE,{"disambiguationData":[TD([[makeQuery(id+"F0.imprint","IMPRINT",EDGE,{"disambiguationData":[TD([[subQ6,1.0]])],"derivedFrom":subQ4}),-1.0]])]});}
            var Q12;
            {var subQ3=sQuery(id+"F0.wireOp",EDGE,"E72");Q12=makeQuery(id+"F0.imprint","IMPRINT",FACE,{"disambiguationData":[TD([[makeQuery(id+"F0.imprint","IMPRINT",EDGE,{"derivedFrom":subQ3}),-1.0]])]});}
            var Q13;
            {var subQ5=sQuery(id+"F0.wireOp",EDGE,"E73");Q13=makeQuery(id+"F0.imprint","IMPRINT",FACE,{"disambiguationData":[TD([[makeQuery(id+"F0.imprint","IMPRINT",EDGE,{"derivedFrom":subQ5}),1.0]])]});}
            var Q14;
            Q14=makeQuery(id+"F0.imprint","IMPRINT",FACE,{"disambiguationData":[TD([[makeQuery(id+"F0.imprint","IMPRINT",EDGE,{"derivedFrom":sQuery(id+"F0.wireOp",EDGE,"E6")}),-1.0]])]});
            var Q15;
            Q15=makeQuery(id+"F0.imprint","IMPRINT",FACE,{"disambiguationData":[TD([[makeQuery(id+"F0.imprint","IMPRINT",EDGE,{"derivedFrom":sQuery(id+"F0.wireOp",EDGE,"E3")}),-1.0]])]});
            extrude(context, id + "F3", {"entities" : qUnion([Q0, Q1, Q2, Q3, Q4, Q5, Q6, Q7, Q8, Q9, Q10, Q11, Q12, Q13, Q14, Q15]), "depth" : 6.6 * mm, "offsetDistance" : 25 * mm});
        }
        {
            var Q0;
            {var subQ9=sQuery(id+"F0.wireOp",EDGE,"E37");Q0=makeQuery(id+"F0.imprint","IMPRINT",FACE,{"disambiguationData":[TD([[makeQuery(id+"F0.imprint","IMPRINT",EDGE,{"derivedFrom":subQ9}),1.0]])]});}
            var Q1;
            {var subQ9=sQuery(id+"F0.wireOp",EDGE,"E29");Q1=makeQuery(id+"F0.imprint","IMPRINT",FACE,{"disambiguationData":[TD([[makeQuery(id+"F0.imprint","IMPRINT",EDGE,{"derivedFrom":subQ9}),-1.0]])]});}
            var Q2;
            {var subQ1=sQuery(id+"F0.wireOp",EDGE,"E28");var subQ5=sQuery(id+"F0.wireOp",EDGE,"E27");var subQ7=makeQuery(id+"F0.imprint","INTERSECT",VERTEX,{"disambiguationData":[OD(1.0)],"derivedFrom":[subQ5,subQ1]});Q2=makeQuery(id+"F0.imprint","IMPRINT",FACE,{"disambiguationData":[TD([[makeQuery(id+"F0.imprint","IMPRINT",EDGE,{"disambiguationData":[TD([[subQ7,1.0]])],"derivedFrom":subQ5}),1.0]])]});}
            var Q3;
            {var subQ5=sQuery(id+"F0.wireOp",EDGE,"E72");Q3=makeQuery(id+"F0.imprint","IMPRINT",FACE,{"disambiguationData":[TD([[makeQuery(id+"F0.imprint","IMPRINT",EDGE,{"derivedFrom":subQ5}),1.0]])]});}
            var Q4;
            {var subQ0=sQuery(id+"F0.wireOp",EDGE,"E1");Q4=makeQuery(id+"F0.imprint","IMPRINT",FACE,{"disambiguationData":[TD([[makeQuery(id+"F0.imprint","IMPRINT",EDGE,{"derivedFrom":subQ0}),1.0]])]});}
            var Q5;
            {var subQ3=sQuery(id+"F0.wireOp",EDGE,"E81");Q5=makeQuery(id+"F0.imprint","IMPRINT",FACE,{"disambiguationData":[TD([[makeQuery(id+"F0.imprint","IMPRINT",EDGE,{"derivedFrom":subQ3}),1.0]])]});}
            var Q6;
            {var subQ14=sQuery(id+"F0.wireOp",EDGE,"E52");Q6=makeQuery(id+"F0.imprint","IMPRINT",FACE,{"disambiguationData":[TD([[makeQuery(id+"F0.imprint","IMPRINT",EDGE,{"derivedFrom":subQ14}),1.0]])]});}
            var Q7;
            {var subQ0=sQuery(id+"F0.wireOp",EDGE,"E20");Q7=makeQuery(id+"F0.imprint","IMPRINT",FACE,{"disambiguationData":[TD([[makeQuery(id+"F0.imprint","IMPRINT",EDGE,{"derivedFrom":subQ0}),1.0]])]});}
            var Q8;
            Q8=makeQuery(id+"F0.imprint","IMPRINT",FACE,{"disambiguationData":[TD([[makeQuery(id+"F0.imprint","IMPRINT",EDGE,{"derivedFrom":sQuery(id+"F0.wireOp",EDGE,"E4")}),-1.0]])]});
            var Q9;
            Q9=makeQuery(id+"F0.imprint","IMPRINT",FACE,{"disambiguationData":[TD([[makeQuery(id+"F0.imprint","IMPRINT",EDGE,{"derivedFrom":sQuery(id+"F0.wireOp",EDGE,"E7")}),-1.0]])]});
            extrude(context, id + "F4", {"entities" : qUnion([Q0, Q1, Q2, Q3, Q4, Q5, Q6, Q7, Q8, Q9]), "depth" : 6.4 * mm, "offsetDistance" : 25 * mm});
        }
        {
            var Q0;
            {var subQ5=sQuery(id+"F0.wireOp",EDGE,"E35");Q0=makeQuery(id+"F0.imprint","IMPRINT",FACE,{"disambiguationData":[TD([[makeQuery(id+"F0.imprint","IMPRINT",EDGE,{"derivedFrom":subQ5}),-1.0]])]});}
            var Q1;
            {var subQ10=sQuery(id+"F0.wireOp",EDGE,"E26");Q1=makeQuery(id+"F0.imprint","IMPRINT",FACE,{"disambiguationData":[TD([[makeQuery(id+"F0.imprint","IMPRINT",EDGE,{"derivedFrom":subQ10}),-1.0]])]});}
            var Q2;
            {var subQ1=sQuery(id+"F0.wireOp",EDGE,"E19");Q2=makeQuery(id+"F0.imprint","IMPRINT",FACE,{"disambiguationData":[TD([[makeQuery(id+"F0.imprint","IMPRINT",EDGE,{"derivedFrom":subQ1}),1.0]])]});}
            var Q3;
            Q3=makeQuery(id+"F0.imprint","IMPRINT",FACE,{"disambiguationData":[TD([[makeQuery(id+"F0.imprint","IMPRINT",EDGE,{"derivedFrom":sQuery(id+"F0.wireOp",EDGE,"E8")}),-1.0]])]});
            var Q4;
            Q4=makeQuery(id+"F0.imprint","IMPRINT",FACE,{"disambiguationData":[TD([[makeQuery(id+"F0.imprint","IMPRINT",EDGE,{"derivedFrom":sQuery(id+"F0.wireOp",EDGE,"E5")}),-1.0]])]});
            var Q5;
            {var subQ6=sQuery(id+"F0.wireOp",EDGE,"E89");Q5=makeQuery(id+"F0.imprint","IMPRINT",FACE,{"disambiguationData":[TD([[makeQuery(id+"F0.imprint","IMPRINT",EDGE,{"derivedFrom":subQ6}),-1.0]])]});}
            var Q6;
            {var subQ6=sQuery(id+"F0.wireOp",EDGE,"E45");var subQ10=sQuery(id+"F0.wireOp",EDGE,"E44");var subQ11=makeQuery(id+"F0.imprint","INTERSECT",VERTEX,{"disambiguationData":[OD(1.0)],"derivedFrom":[subQ10,subQ6]});Q6=makeQuery(id+"F0.imprint","IMPRINT",FACE,{"disambiguationData":[TD([[makeQuery(id+"F0.imprint","IMPRINT",EDGE,{"disambiguationData":[TD([[subQ11,1.0]])],"derivedFrom":subQ10}),1.0]])]});}
            var Q7;
            {var subQ2=sQuery(id+"F0.wireOp",EDGE,"E81");Q7=makeQuery(id+"F0.imprint","IMPRINT",FACE,{"disambiguationData":[TD([[makeQuery(id+"F0.imprint","IMPRINT",EDGE,{"derivedFrom":subQ2}),-1.0]])]});}
            var Q8;
            {var subQ0=sQuery(id+"F0.wireOp",EDGE,"E51");Q8=makeQuery(id+"F0.imprint","IMPRINT",FACE,{"disambiguationData":[TD([[makeQuery(id+"F0.imprint","IMPRINT",EDGE,{"derivedFrom":subQ0}),1.0]])]});}
            var Q9;
            Q9=makeQuery(id+"F0.imprint","IMPRINT",FACE,{"disambiguationData":[TD([[makeQuery(id+"F0.imprint","IMPRINT",EDGE,{"derivedFrom":sQuery(id+"F0.wireOp",EDGE,"E58")}),-1.0]])]});
            var Q10;
            Q10=makeQuery(id+"F0.imprint","IMPRINT",FACE,{"disambiguationData":[TD([[makeQuery(id+"F0.imprint","IMPRINT",EDGE,{"derivedFrom":sQuery(id+"F0.wireOp",EDGE,"E59")}),-1.0]])]});
            extrude(context, id + "F5", {"entities" : qUnion([Q0, Q1, Q2, Q3, Q4, Q5, Q6, Q7, Q8, Q9, Q10]), "depth" : 6.2 * mm, "offsetDistance" : 25 * mm});
        }
        {
            var Q0;
            {var subQ2=sQuery(id+"F0.wireOp",EDGE,"E83");Q0=makeQuery(id+"F0.imprint","IMPRINT",FACE,{"disambiguationData":[TD([[makeQuery(id+"F0.imprint","IMPRINT",EDGE,{"derivedFrom":subQ2}),-1.0]])]});}
            var Q1;
            {var subQ4=sQuery(id+"F0.wireOp",EDGE,"E48");Q1=makeQuery(id+"F0.imprint","IMPRINT",FACE,{"disambiguationData":[TD([[makeQuery(id+"F0.imprint","IMPRINT",EDGE,{"derivedFrom":subQ4}),1.0]])]});}
            var Q2;
            {var subQ6=sQuery(id+"F0.wireOp",EDGE,"E90");Q2=makeQuery(id+"F0.imprint","IMPRINT",FACE,{"disambiguationData":[TD([[makeQuery(id+"F0.imprint","IMPRINT",EDGE,{"derivedFrom":subQ6}),1.0]])]});}
            var Q3;
            Q3=makeQuery(id+"F0.imprint","IMPRINT",FACE,{"disambiguationData":[TD([[makeQuery(id+"F0.imprint","IMPRINT",EDGE,{"derivedFrom":sQuery(id+"F0.wireOp",EDGE,"E58")}),1.0]])]});
            var Q4;
            Q4=makeQuery(id+"F0.imprint","IMPRINT",FACE,{"disambiguationData":[TD([[makeQuery(id+"F0.imprint","IMPRINT",EDGE,{"derivedFrom":sQuery(id+"F0.wireOp",EDGE,"E59")}),1.0]])]});
            var Q5;
            {var subQ4=sQuery(id+"F0.wireOp",EDGE,"E64");Q5=makeQuery(id+"F0.imprint","IMPRINT",FACE,{"disambiguationData":[TD([[makeQuery(id+"F0.imprint","IMPRINT",EDGE,{"derivedFrom":subQ4}),1.0]])]});}
            var Q6;
            {var subQ5=sQuery(id+"F0.wireOp",EDGE,"E66");Q6=makeQuery(id+"F0.imprint","IMPRINT",FACE,{"disambiguationData":[TD([[makeQuery(id+"F0.imprint","IMPRINT",EDGE,{"derivedFrom":subQ5}),1.0]])]});}
            extrude(context, id + "F6", {"entities" : qUnion([Q0, Q1, Q2, Q3, Q4, Q5, Q6]), "depth" : 6 * mm, "offsetDistance" : 25 * mm});
        }
        {
            var Q0;
            {var subQ7=sQuery(id+"F0.wireOp",EDGE,"E26");Q0=makeQuery(id+"F0.imprint","IMPRINT",FACE,{"disambiguationData":[TD([[makeQuery(id+"F0.imprint","IMPRINT",EDGE,{"derivedFrom":subQ7}),1.0]])]});}
            var Q1;
            {var subQ0=sQuery(id+"F0.wireOp",EDGE,"E87");Q1=makeQuery(id+"F0.imprint","IMPRINT",FACE,{"disambiguationData":[TD([[makeQuery(id+"F0.imprint","IMPRINT",EDGE,{"derivedFrom":subQ0}),1.0]])]});}
            var Q2;
            {var subQ0=sQuery(id+"F0.wireOp",EDGE,"E54");var subQ1=sQuery(id+"F0.wireOp",EDGE,"E53");var subQ2=makeQuery(id+"F0.imprint","INTERSECT",VERTEX,{"disambiguationData":[OD(0.0)],"derivedFrom":[subQ1,subQ0]});Q2=makeQuery(id+"F0.imprint","IMPRINT",FACE,{"disambiguationData":[TD([[makeQuery(id+"F0.imprint","IMPRINT",EDGE,{"disambiguationData":[TD([[subQ2,1.0]])],"derivedFrom":subQ1}),1.0]])]});}
            var Q3;
            {var subQ5=sQuery(id+"F0.wireOp",EDGE,"E62");Q3=makeQuery(id+"F0.imprint","IMPRINT",FACE,{"disambiguationData":[TD([[makeQuery(id+"F0.imprint","IMPRINT",EDGE,{"derivedFrom":subQ5}),-1.0]])]});}
            var Q4;
            {var subQ3=sQuery(id+"F0.wireOp",EDGE,"E86");Q4=makeQuery(id+"F0.imprint","IMPRINT",FACE,{"disambiguationData":[TD([[makeQuery(id+"F0.imprint","IMPRINT",EDGE,{"derivedFrom":subQ3}),1.0]])]});}
            extrude(context, id + "F7", {"entities" : qUnion([Q0, Q1, Q2, Q3, Q4]), "depth" : 5.8 * mm, "offsetDistance" : 25 * mm});
        }
        {
            var Q0;
            {var subQ3=sQuery(id+"F0.wireOp",EDGE,"E91");Q0=makeQuery(id+"F0.imprint","IMPRINT",FACE,{"disambiguationData":[TD([[makeQuery(id+"F0.imprint","IMPRINT",EDGE,{"derivedFrom":subQ3}),1.0]])]});}
            var Q1;
            {var subQ3=sQuery(id+"F0.wireOp",EDGE,"E67");Q1=makeQuery(id+"F0.imprint","IMPRINT",FACE,{"disambiguationData":[TD([[makeQuery(id+"F0.imprint","IMPRINT",EDGE,{"derivedFrom":subQ3}),-1.0]])]});}
            var Q2;
            {var subQ3=sQuery(id+"F0.wireOp",EDGE,"E84");Q2=makeQuery(id+"F0.imprint","IMPRINT",FACE,{"disambiguationData":[TD([[makeQuery(id+"F0.imprint","IMPRINT",EDGE,{"derivedFrom":subQ3}),-1.0]])]});}
            var Q3;
            {var subQ0=sQuery(id+"F0.wireOp",EDGE,"E85");Q3=makeQuery(id+"F0.imprint","IMPRINT",FACE,{"disambiguationData":[TD([[makeQuery(id+"F0.imprint","IMPRINT",EDGE,{"derivedFrom":subQ0}),1.0]])]});}
            extrude(context, id + "F8", {"entities" : qUnion([Q0, Q1, Q2, Q3]), "depth" : 5.6 * mm, "offsetDistance" : 25 * mm});
        }
        {
            var Q0;
            {var subQ0=sQuery(id+"F0.wireOp",EDGE,"E82");var subQ1=sQuery(id+"F0.wireOp",EDGE,"E70");var subQ2=makeQuery(id+"F0.imprint","INTERSECT",VERTEX,{"derivedFrom":[subQ1,subQ0]});Q0=makeQuery(id+"F0.imprint","IMPRINT",FACE,{"disambiguationData":[TD([[makeQuery(id+"F0.imprint","IMPRINT",EDGE,{"disambiguationData":[TD([[subQ2,1.0]])],"derivedFrom":subQ1}),-1.0]])]});}
            var Q1;
            {var subQ2=sQuery(id+"F0.wireOp",EDGE,"E56");Q1=makeQuery(id+"F0.imprint","IMPRINT",FACE,{"disambiguationData":[TD([[makeQuery(id+"F0.imprint","IMPRINT",EDGE,{"derivedFrom":subQ2}),-1.0]])]});}
            var Q2;
            {var subQ0=sQuery(id+"F0.wireOp",EDGE,"E83");var subQ1=sQuery(id+"F0.wireOp",EDGE,"E82");var subQ2=makeQuery(id+"F0.imprint","INTERSECT",VERTEX,{"disambiguationData":[OD(1.0)],"derivedFrom":[subQ1,subQ0]});Q2=makeQuery(id+"F0.imprint","IMPRINT",FACE,{"disambiguationData":[TD([[makeQuery(id+"F0.imprint","IMPRINT",EDGE,{"disambiguationData":[TD([[subQ2,-1.0]])],"derivedFrom":subQ1}),-1.0]])]});}
            extrude(context, id + "F9", {"entities" : qUnion([Q0, Q1, Q2]), "depth" : 5.6 * mm, "offsetDistance" : 25 * mm});
        }
        {
            var Q0;
            {var subQ3=sQuery(id+"F0.wireOp",EDGE,"E64");Q0=makeQuery(id+"F0.imprint","IMPRINT",FACE,{"disambiguationData":[TD([[makeQuery(id+"F0.imprint","IMPRINT",EDGE,{"derivedFrom":subQ3}),-1.0]])]});}
            extrude(context, id + "F10", {"entities" : qUnion([Q0]), "depth" : 5.4 * mm, "offsetDistance" : 25 * mm});
        }
        {
            var Q0;
            Q0=qCreatedBy(makeId("Top.planeOp"),FACE);
            var sketch = newSketch(context, id + "F11", { "sketchPlane" : qUnion([Q0])});
            skLineSegment(sketch, "E92.bottom", {"start": v(-9.97, 21.54) * mm, "end": v(9.03, 21.54) * mm});
            skLineSegment(sketch, "E92.top", {"start": v(-9.97, -21.46) * mm, "end": v(9.03, -21.46) * mm});
            skLineSegment(sketch, "E92.left", {"start": v(-14.97, 16.54) * mm, "end": v(-14.97, -16.46) * mm});
            skLineSegment(sketch, "E92.right", {"start": v(14.03, 16.54) * mm, "end": v(14.03, -16.46) * mm});
            skLineSegment(sketch, "E93.bottom", {"start": v(-9.97, 23.54) * mm, "end": v(9.03, 23.54) * mm});
            skLineSegment(sketch, "E93.top", {"start": v(-15.97, -31.46) * mm, "end": v(9.03, -31.46) * mm});
            skLineSegment(sketch, "E93.left", {"start": v(-16.97, 16.54) * mm, "end": v(-16.97, -30.46) * mm});
            skLineSegment(sketch, "E93.right", {"start": v(16.03, 16.54) * mm, "end": v(16.03, -24.46) * mm});
            skPoint(sketch, "E94.visualSharp", {"position": v(-14.97, 21.54) * mm});
            skArc(sketch, "E94.filletArc", {"start": v(-9.97, 21.54) * mm, "mid": v(-13.5, 20.07) * mm, "end": v(-14.97, 16.54) * mm});
            skPoint(sketch, "E95.visualSharp", {"position": v(14.03, 21.54) * mm});
            skArc(sketch, "E95.filletArc", {"start": v(14.03, 16.54) * mm, "mid": v(12.56, 20.07) * mm, "end": v(9.03, 21.54) * mm});
            skPoint(sketch, "E96.visualSharp", {"position": v(14.03, -21.46) * mm});
            skArc(sketch, "E96.filletArc", {"start": v(9.03, -21.46) * mm, "mid": v(12.56, -20) * mm, "end": v(14.03, -16.46) * mm});
            skPoint(sketch, "E97.visualSharp", {"position": v(16.03, 23.54) * mm});
            skArc(sketch, "E97.filletArc", {"start": v(16.03, 16.54) * mm, "mid": v(13.98, 21.49) * mm, "end": v(9.03, 23.54) * mm});
            skPoint(sketch, "E98.visualSharp", {"position": v(16.03, -31.46) * mm});
            skArc(sketch, "E98.filletArc", {"start": v(9.03, -31.46) * mm, "mid": v(13.98, -29.41) * mm, "end": v(16.03, -24.46) * mm});
            skPoint(sketch, "E99.visualSharp", {"position": v(-16.97, 23.54) * mm});
            skArc(sketch, "E99.filletArc", {"start": v(-9.97, 23.54) * mm, "mid": v(-14.92, 21.49) * mm, "end": v(-16.97, 16.54) * mm});
            skPoint(sketch, "E100.visualSharp", {"position": v(-14.97, -21.46) * mm});
            skArc(sketch, "E100.filletArc", {"start": v(-14.97, -16.46) * mm, "mid": v(-13.5, -20) * mm, "end": v(-9.97, -21.46) * mm});
            skPoint(sketch, "E101.visualSharp", {"position": v(-16.97, -31.46) * mm});
            skArc(sketch, "E101.filletArc", {"start": v(-16.97, -30.46) * mm, "mid": v(-16.68, -31.17) * mm, "end": v(-15.97, -31.46) * mm});
            skCircle(sketch, "E102", {"center": v(0, 33.54) * mm, "radius": 6 * mm});
            skCircle(sketch, "E103", {"center": v(0, 33.54) * mm, "radius": 4 * mm});
            skArc(sketch, "E104", {"start": v(-8.98, 23.54) * mm, "mid": v(-5.3, 26.22) * mm, "end": v(-5.32, 30.77) * mm});
            skLineSegment(sketch, "E105.bottom", {"start": v(-3.1, 27.24) * mm, "end": v(3.1, 27.24) * mm});
            skLineSegment(sketch, "E105.top", {"start": v(-4.1, 23.54) * mm, "end": v(4.1, 23.54) * mm});
            skLineSegment(sketch, "E105.left", {"start": v(-4.1, 26.24) * mm, "end": v(-4.1, 23.54) * mm});
            skLineSegment(sketch, "E105.right", {"start": v(4.1, 26.24) * mm, "end": v(4.1, 23.54) * mm});
            skPoint(sketch, "E106.visualSharp", {"position": v(-4.1, 27.24) * mm});
            skArc(sketch, "E106.filletArc", {"start": v(-3.1, 27.24) * mm, "mid": v(-3.8, 26.95) * mm, "end": v(-4.1, 26.24) * mm});
            skPoint(sketch, "E107.visualSharp", {"position": v(4.1, 27.24) * mm});
            skArc(sketch, "E107.filletArc", {"start": v(4.1, 26.24) * mm, "mid": v(3.8, 26.95) * mm, "end": v(3.1, 27.24) * mm});
            skArc(sketch, "E108", {"start": v(5.41, 30.95) * mm, "mid": v(5.75, 26.53) * mm, "end": v(9.03, 23.54) * mm});
            skSolve(sketch);
        }
        {
            var Q0;
            Q0=makeQuery(id+"F11.imprint","IMPRINT",FACE,{"disambiguationData":[TD([[makeQuery(id+"F11.imprint","IMPRINT",EDGE,{"derivedFrom":sQuery(id+"F11.wireOp",EDGE,"E92.bottom")}),1.0]])]});
            extrude(context, id + "F12", {"entities" : qUnion([Q0]), "depth" : 6 * mm, "offsetDistance" : 25 * mm});
        }
        {
            var Q0;
            Q0=makeQuery(id+"F12.opExtrude","CAP_FACE",FACE,{"disambiguationData":[OSD([sQuery(id+"F11.wireOp",EDGE,"E92.bottom"),sQuery(id+"F11.wireOp",EDGE,"E92.top"),sQuery(id+"F11.wireOp",EDGE,"E92.left"),sQuery(id+"F11.wireOp",EDGE,"E92.right"),sQuery(id+"F11.wireOp",EDGE,"E93.bottom"),sQuery(id+"F11.wireOp",EDGE,"E93.top"),sQuery(id+"F11.wireOp",EDGE,"E93.left"),sQuery(id+"F11.wireOp",EDGE,"E93.right"),sQuery(id+"F11.wireOp",EDGE,"E94.filletArc"),sQuery(id+"F11.wireOp",EDGE,"E95.filletArc"),sQuery(id+"F11.wireOp",EDGE,"E96.filletArc"),sQuery(id+"F11.wireOp",EDGE,"E97.filletArc"),sQuery(id+"F11.wireOp",EDGE,"E98.filletArc"),sQuery(id+"F11.wireOp",EDGE,"E99.filletArc"),sQuery(id+"F11.wireOp",EDGE,"E100.filletArc"),sQuery(id+"F11.wireOp",EDGE,"E101.filletArc")])],"isStart":false});
            var sketch = newSketch(context, id + "F13", { "sketchPlane" : qUnion([Q0])});
            skText(sketch, "E109", { "text": "СОШ №16", "fontName": "OpenSans-Bold.ttf"});
            const initialGuessF13  = {"E109": [-0.01527, -0.02801, 1, 0, 0.00416]};
            skSetInitialGuess(sketch, initialGuessF13);
            skSolve(sketch);
        }
        {
            var Q0;
            Q0=qSketchRegion(id+"F13",true);
            extrude(context, id + "F14", {"entities" : qUnion([Q0]), "operationType" : NewBodyOperationType.ADD, "depth" : 0.4 * mm, "offsetDistance" : 25 * mm});
        }
        {
            var Q0;
            Q0=makeQuery(id+"F12.opExtrude","CAP_EDGE",EDGE,{"disambiguationData":[OSD([sQuery(id+"F11.wireOp",EDGE,"E98.filletArc")])],"isStart":false});
            fillet(context, id + "F15", {"entities" : qUnion([Q0]), "radius" : 1.5 * mm, "tangentPropagation" : true, "allowEdgeOverflow" : false});
        }
        {
            var Q0;
            Q0=makeQuery(id+"F11.imprint","IMPRINT",FACE,{"disambiguationData":[TD([[makeQuery(id+"F11.imprint","IMPRINT",EDGE,{"derivedFrom":sQuery(id+"F11.wireOp",EDGE,"E103")}),-1.0]])]});
            extrude(context, id + "F16", {"entities" : qUnion([Q0]), "depth" : 6 * mm, "offsetDistance" : 25 * mm});
        }
        {
            var Q0;
            {var subQ0=sQuery(id+"F11.wireOp",EDGE,"E104");Q0=makeQuery(id+"F11.imprint","IMPRINT",FACE,{"disambiguationData":[TD([[makeQuery(id+"F11.imprint","IMPRINT",EDGE,{"derivedFrom":subQ0}),-1.0]])]});}
            extrude(context, id + "F17", {"entities" : qUnion([Q0]), "depth" : 4.4 * mm, "offsetDistance" : 25 * mm});
        }
        {
            var Q0;
            Q0=makeQuery(id+"F16.opExtrude","CAP_FACE",FACE,{"disambiguationData":[OSD([sQuery(id+"F11.wireOp",EDGE,"E102"),sQuery(id+"F11.wireOp",EDGE,"E103")])],"isStart":false});
            fillet(context, id + "F18", {"entities" : qUnion([Q0]), "radius" : 1 * mm, "tangentPropagation" : true, "allowEdgeOverflow" : false});
        }
        {
            var Q0;
            Q0=makeQuery(id+"F17.opExtrude","CAP_EDGE",EDGE,{"disambiguationData":[OSD([sQuery(id+"F11.wireOp",EDGE,"aUvm8erm-xxqf-If5a-6mQM-qNdrGN8eYJHd")])],"isStart":false});
            var Q1;
            Q1=makeQuery(id+"F17.opExtrude","CAP_EDGE",EDGE,{"disambiguationData":[OSD([sQuery(id+"F11.wireOp",EDGE,"E104")])],"isStart":false});
            var Q2;
            Q2=makeQuery(id+"F17.opExtrude","CAP_EDGE",EDGE,{"disambiguationData":[OSD([sQuery(id+"F11.wireOp",EDGE,"E108")])],"isStart":false});
            fillet(context, id + "F19", {"entities" : qUnion([Q0, Q1, Q2]), "radius" : 1 * mm, "tangentPropagation" : true, "allowEdgeOverflow" : false});
        }
        {
            var Q0;
            Q0=makeQuery(id+"F12.opExtrude","SWEPT_FACE",FACE,{"disambiguationData":[OSD([sQuery(id+"F11.wireOp",EDGE,"E92.bottom")])]});
            var sketch = newSketch(context, id + "F20", { "sketchPlane" : qUnion([Q0])});
            skCircle(sketch, "E110", {"center": v(0, 2.8) * mm, "radius": 1.5 * mm});
            skSolve(sketch);
        }
        {
            var Q0;
            Q0=makeQuery(id+"F20.imprint","IMPRINT",FACE,{"disambiguationData":[TD([[makeQuery(id+"F20.imprint","IMPRINT",EDGE,{"derivedFrom":sQuery(id+"F20.wireOp",EDGE,"E110")}),-1.0]])]});
            var sketch = newSketch(context, id + "F21", { "sketchPlane" : qUnion([Q0])});
            skCircle(sketch, "E111", {"center": v(0, 2.8) * mm, "radius": 1.8 * mm});
            skSolve(sketch);
        }
        {
            var Q0;
            Q0=qSketchRegion(id+"F21",true);
            extrude(context, id + "F22", {"entities" : qUnion([Q0]), "operationType" : NewBodyOperationType.REMOVE, "oppositeDirection" : true, "depth" : 3 * mm, "offsetDistance" : 25 * mm});
        }
        {
            var Q0;
            Q0=makeQuery(id+"F20.imprint","IMPRINT",FACE,{"disambiguationData":[TD([[makeQuery(id+"F20.imprint","IMPRINT",EDGE,{"derivedFrom":sQuery(id+"F20.wireOp",EDGE,"E110")}),1.0]])]});
            var Q1;
            Q1=sQuery(id+"F20.wireOp",EDGE,"E110");
            extrude(context, id + "F23", {"entities" : qUnion([Q0]), "surfaceEntities" : qUnion([Q1]), "depth" : 7 * mm, "offsetDistance" : 25 * mm, "hasSecondDirection" : true, "secondDirectionOppositeDirection" : true, "secondDirectionDepth" : 4 * mm});
        }
        {
            var Q0;
            Q0=qCreatedBy(makeId("Top.planeOp"),FACE);
            var sketch = newSketch(context, id + "F24", { "sketchPlane" : qUnion([Q0])});
            skLineSegment(sketch, "E112.bottom", {"start": v(2.4, 24.17) * mm, "end": v(-2.4, 24.17) * mm});
            skLineSegment(sketch, "E112.top", {"start": v(2.4, 26.47) * mm, "end": v(-2.4, 26.47) * mm});
            skLineSegment(sketch, "E112.left", {"start": v(2.4, 24.17) * mm, "end": v(2.4, 26.47) * mm});
            skLineSegment(sketch, "E112.right", {"start": v(-2.4, 24.17) * mm, "end": v(-2.4, 26.47) * mm});
            skPoint(sketch, "E112.middle", {"position": v(0, 25.32) * mm});
            skSolve(sketch);
        }
        {
            var Q0;
            Q0=makeQuery(id+"F24.imprint","IMPRINT",FACE,{"disambiguationData":[TD([[makeQuery(id+"F24.imprint","IMPRINT",EDGE,{"derivedFrom":sQuery(id+"F24.wireOp",EDGE,"E112.bottom")}),-1.0]])]});
            extrude(context, id + "F25", {"entities" : qUnion([Q0]), "operationType" : NewBodyOperationType.ADD, "depth" : 5 * mm, "offsetDistance" : 25 * mm});
        }
        {
            var Q0;
            Q0=makeQuery(id+"F25.opExtrude","CAP_EDGE",EDGE,{"disambiguationData":[OSD([sQuery(id+"F24.wireOp",EDGE,"E112.right")])],"isStart":false});
            var Q1;
            Q1=makeQuery(id+"F25.opExtrude","CAP_EDGE",EDGE,{"disambiguationData":[OSD([sQuery(id+"F24.wireOp",EDGE,"E112.left")])],"isStart":false});
            var Q2;
            Q2=makeQuery(id+"F25.opExtrude","CAP_EDGE",EDGE,{"disambiguationData":[OSD([sQuery(id+"F24.wireOp",EDGE,"E112.right")])],"isStart":true});
            var Q3;
            Q3=makeQuery(id+"F25.opExtrude","CAP_EDGE",EDGE,{"disambiguationData":[OSD([sQuery(id+"F24.wireOp",EDGE,"E112.left")])],"isStart":true});
            fillet(context, id + "F26", {"entities" : qUnion([Q0, Q1, Q2, Q3]), "radius" : 1 * mm, "tangentPropagation" : true, "allowEdgeOverflow" : false});
        }
    });
